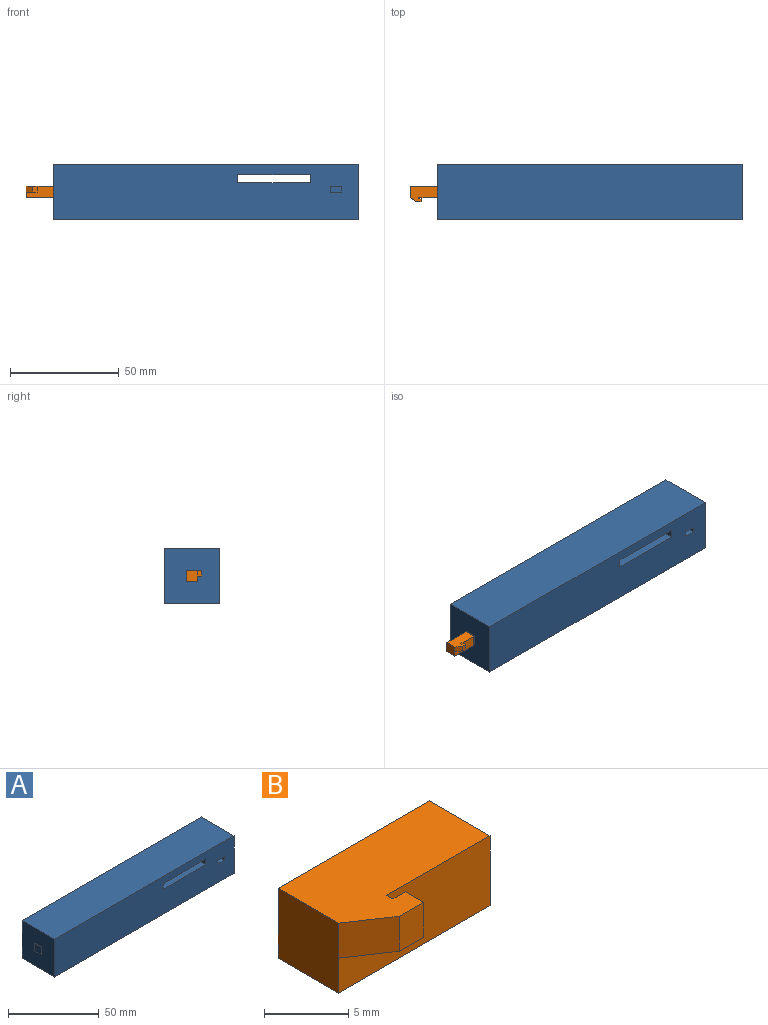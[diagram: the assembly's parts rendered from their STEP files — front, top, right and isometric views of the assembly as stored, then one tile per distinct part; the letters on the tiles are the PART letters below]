
ASSEMBLY  parts=2 mates=1
PART A: 22 faces, bbox 140x25.4x25.4 mm
  f0: plane 25.4x25.4mm, normal (-1,0,0), area 619.4mm2, adj f1,f2,f4,f5,f17,f18,f19,f20
  f1: plane 139.7x25.4mm, normal (0,0,1), area 3548.4mm2, adj f0,f3,f4,f5
  f2: plane 139.7x25.4mm, normal (0,0,-1), area 3548.4mm2, adj f0,f3,f4,f5
  f3: plane 25.4x25.4mm, normal (1,0,0), area 619.4mm2, adj f1,f2,f4,f5,f6,f7,f8,f9
  f4: plane 139.7x25.4mm, normal (0,1,0), area 3422.9mm2, adj f0,f1,f2,f3,f13,f14,f15,f16
  f5: plane 139.7x25.4mm, normal (0,-1,0), area 3410mm2, adj f0,f1,f2,f3,f7,f10,f11,f12
  f6: plane 12.7x5.08mm, normal (0,-1,0), area 64.5mm2, adj f3,f7,f9,f10
  f7: plane 15.24x12.7mm, normal (0,0,-1), area 116.1mm2, adj f3,f5,f6,f8,f10,f11
  f8: plane 12.7x5.08mm, normal (0,1,0), area 51.6mm2, adj f3,f7,f9,f10,f11,f12
  f9: plane 12.7x5.08mm, normal (0,0,1), area 64.5mm2, adj f3,f6,f8,f10
  f10: plane 15.24x5.08mm, normal (1,0,0), area 51.6mm2, adj f5,f6,f7,f8,f9,f12
  f11: plane 10.16x2.54mm, normal (-1,0,0), area 25.8mm2, adj f5,f7,f8,f12
  f12: plane 10.16x5.08mm, normal (0,0,1), area 51.6mm2, adj f5,f8,f10,f11
  f13: plane 25.4x3.75mm, normal (1,0,0), area 95.3mm2, adj f4,f5,f14,f16
  f14: plane 33.45x25.4mm, normal (0,0,1), area 849.5mm2, adj f4,f5,f13,f15
  f15: plane 25.4x3.75mm, normal (-1,0,0), area 95.3mm2, adj f4,f5,f14,f16
  f16: plane 33.45x25.4mm, normal (0,0,-1), area 849.5mm2, adj f4,f5,f13,f15
  f17: plane 5.08x0.25mm, normal (0,0,-1), area 1.3mm2, adj f0,f18,f20,f21
  f18: plane 5.08x0.25mm, normal (0,-1,0), area 1.3mm2, adj f0,f17,f19,f21
  f19: plane 5.08x0.25mm, normal (0,0,1), area 1.3mm2, adj f0,f18,f20,f21
  f20: plane 5.08x0.25mm, normal (0,1,0), area 1.3mm2, adj f0,f17,f19,f21
  f21: plane 5.08x5.08mm, normal (-1,0,0), area 25.8mm2, adj f17,f18,f19,f20
PART B: 12 faces, bbox 12.7x7.1x5.1 mm
  f0: plane 5.07x2.03mm, normal (0,0,-1), area 6.7mm2, adj f1,f2,f3,f4,f5,f10
  f1: plane 2.54x2.03mm, normal (0,-1,0), area 5.2mm2, adj f0,f2,f5,f9
  f2: plane 3.04x2.54mm, normal (-0.56,-0.83,0), area 9.3mm2, adj f0,f1,f6,f9
  f3: plane 2.54x0.51mm, normal (1,0,0), area 1.3mm2, adj f0,f4,f9,f10
  f4: plane 2.54x1.02mm, normal (0,1,0), area 2.6mm2, adj f0,f3,f5,f9
  f5: plane 2.54x1.52mm, normal (1,0,0), area 3.9mm2, adj f0,f1,f4,f9
  f6: plane 5.08x5.08mm, normal (-1,0,0), area 25.8mm2, adj f2,f7,f8,f9,f10
  f7: plane 12.7x5.08mm, normal (0,0,-1), area 64.5mm2, adj f6,f8,f10,f11
  f8: plane 12.7x5.08mm, normal (0,1,0), area 64.5mm2, adj f6,f7,f9,f11
  f9: plane 12.7x7.11mm, normal (0,0,1), area 71.2mm2, adj f1,f2,f3,f4,f5,f6,f8,f10
  f10: plane 12.7x5.08mm, normal (0,-1,0), area 54.2mm2, adj f0,f3,f6,f7,f9,f11
  f11: plane 5.08x5.08mm, normal (1,0,0), area 25.8mm2, adj f7,f8,f9,f10
PLACE A t=(15.47,4.24,-17.58)mm
PLACE B t=(28.17,4.24,-17.58)mm
MATE parallel B.f11 <-> A.f0  axis (1,0,0) through (-48.03,4.24,-4.88)mm
